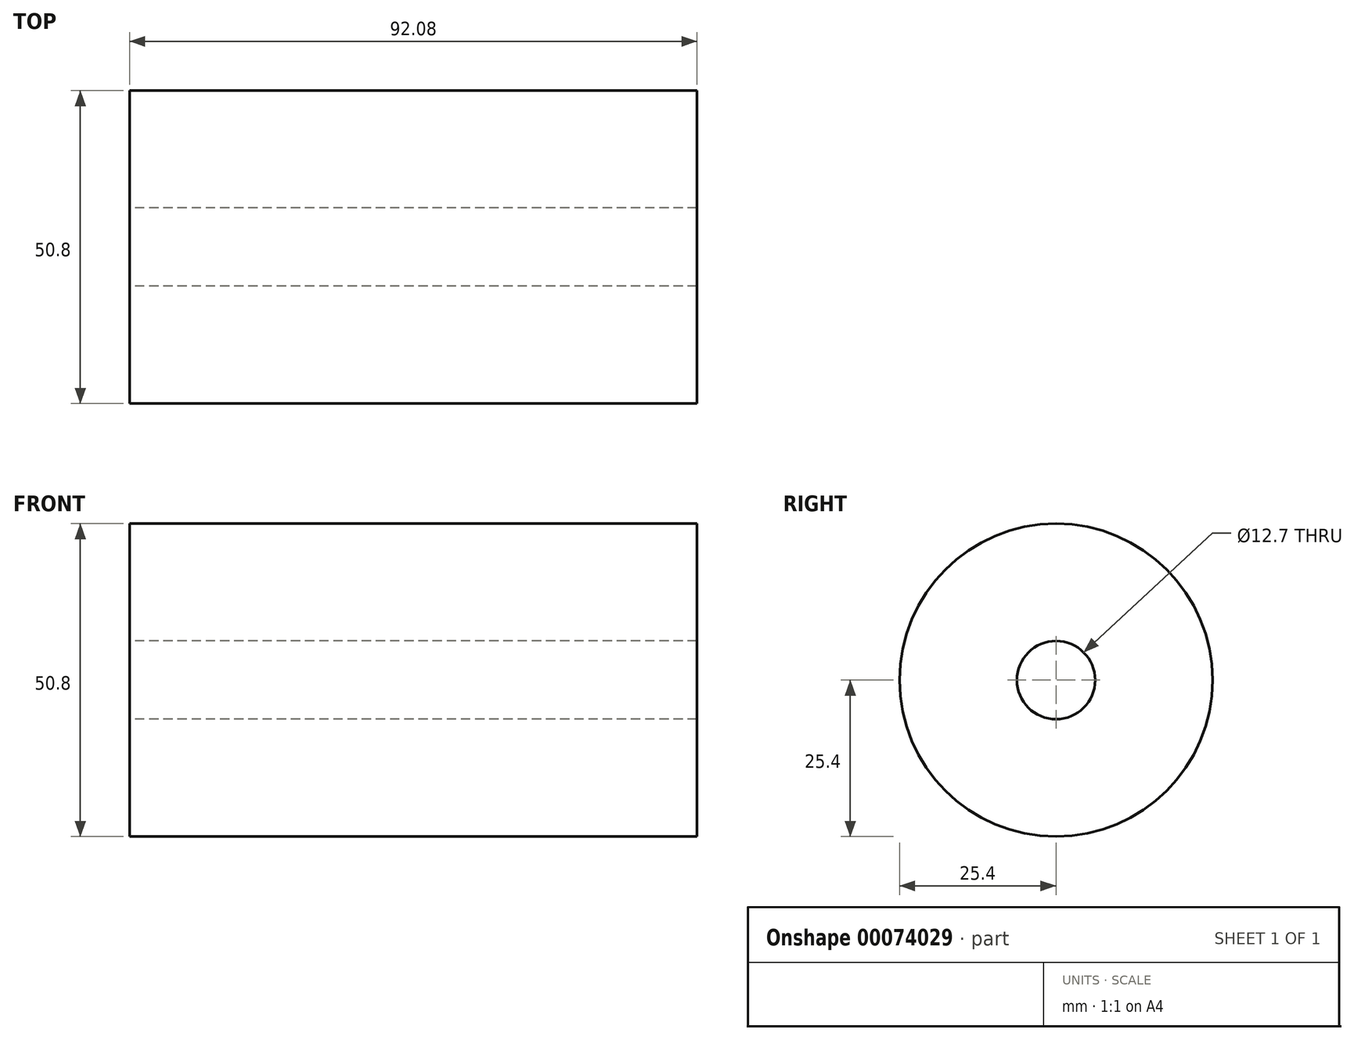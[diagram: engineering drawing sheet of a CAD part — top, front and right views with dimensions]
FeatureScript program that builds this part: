
annotation { "Feature Type Name" : "Feature", "Feature Type Description" : "" }
export const myFeature = defineFeature(function(context is Context, id is Id, definition is map)
    precondition{}
    {
        {
            var Q0;
            Q0=qCreatedBy(makeId("Right.planeOp"),FACE);
            var sketch = newSketch(context, id + "F0", { "sketchPlane" : qUnion([Q0])});
            skCircle(sketch, "E0", {"center": v(0, 0) * mm, "radius": 25.4 * mm});
            skCircle(sketch, "E1", {"center": v(0, 0) * mm, "radius": 6.35 * mm});
            skSolve(sketch);
        }
        {
            var Q0;
            Q0=makeQuery(id+"F0.imprint","IMPRINT",FACE,{"disambiguationData":[TD([[makeQuery(id+"F0.imprint","IMPRINT",EDGE,{"derivedFrom":sQuery(id+"F0.wireOp",EDGE,"E0")}),1.0]])]});
            extrude(context, id + "F1", {"entities" : qUnion([Q0]), "depth" : 92.07 * mm, "symmetric" : true});
        }
    });
